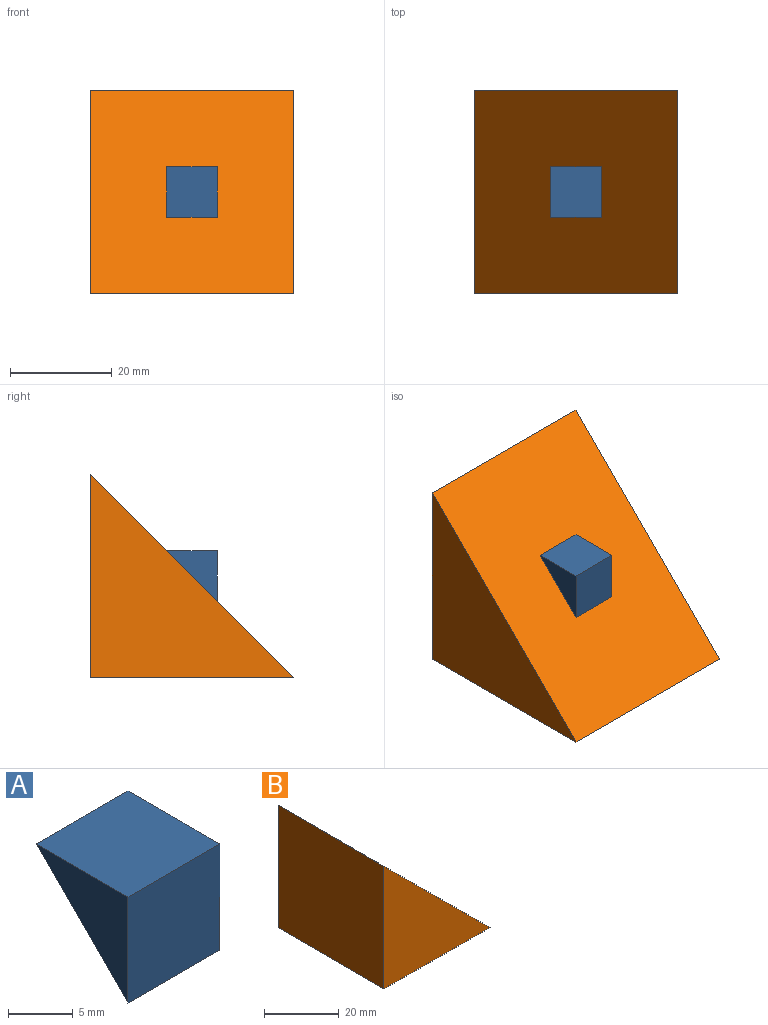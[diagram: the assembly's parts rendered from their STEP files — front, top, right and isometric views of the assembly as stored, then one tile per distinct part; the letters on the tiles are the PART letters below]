
ASSEMBLY  parts=2 mates=1
PART A: 5 faces, bbox 10x10x10 mm
  f0: plane 10x10mm, normal (-1,0,0), area 50mm2, adj f1,f3,f4
  f1: plane 10x10mm, normal (0,-1,0), area 100mm2, adj f0,f2,f3,f4
  f2: plane 10x10mm, normal (1,0,0), area 50mm2, adj f1,f3,f4
  f3: plane 10x10mm, normal (0,0,1), area 100mm2, adj f0,f1,f2,f4
  f4: plane 10x10mm, normal (0,0.71,-0.71), area 141.4mm2, adj f0,f1,f2,f3
PART B: 5 faces, bbox 40x40x40 mm
  f0: plane 40x40mm, normal (0,1,0), area 800mm2, adj f1,f3,f4
  f1: plane 40x40mm, normal (-1,0,0), area 1600mm2, adj f0,f2,f3,f4
  f2: plane 40x40mm, normal (0,-1,0), area 800mm2, adj f1,f3,f4
  f3: plane 40x40mm, normal (0,0,-1), area 1600mm2, adj f0,f1,f2,f4
  f4: plane 40x40mm, normal (0.71,0,0.71), area 2262.7mm2, adj f0,f1,f2,f3
PLACE A t=(-36.23,-17.28,0.45)mm
PLACE B rot(axis=(0,0,-1),90deg) t=(-36.23,-17.28,5.45)mm
MATE planar B.f4 <-> A.f4  axis (0,-0.71,0.71) through (-36.23,-17.28,5.45)mm
